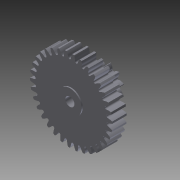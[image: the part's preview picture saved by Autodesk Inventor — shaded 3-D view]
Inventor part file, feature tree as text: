
AUTODESK INVENTOR PART (.ipt)
format: ipt  version: 2013 (Build 170138000, 138)  size: 1,623,040 bytes
history: native  units: in
note: dims shown in document units (in); Inventor stores cm internally (conversion verified against a paired STEP export)
features: extrude x4, sketch x3, plane x1, hole x1, fillet x1, projected_geometry x1
ambient origin geometry x8: Origin, YZ Plane, XZ Plane, XY Plane, X Axis, Y Axis, Z Axis, Center Point
bodies: Solid1 (feature_tree)
feature tree (11):
  sketch  "Sketch1"  dims[d0=0.098in d1=0.0in d2=0.008in d3=0.0in]
  extrude  "Extrusion1"  Depth=0.008in TaperAngle=0.0deg
  extrude  "Extrusion2"  Depth=0.008in TaperAngle=0.0deg
  plane  "Work Plane1"
  sketch  "Sketch2"  dims[d4=0.157in d5=0.008in d6=0.0in]
  extrude  "Extrusion3"  Depth=0.005in
  extrude  "Extrusion4"  [1 undecoded]
  hole  "Hole1"  [1 undecoded]
  fillet  "Fillet1"  [1 undecoded]
  projected_geometry  "Projected Loop1"
  sketch  "Sketch3"  dims[d7=0.008in d8=0.0in d9=0.061in d10=0.75in d11=0.375in d12=0.25in d13=0.5635in d14=1.0in d15=0.8108in d16=0.005in]
note: 3 required parameter values undecoded (feature->parameter linkage not recoverable at this tier; creation-order binding heuristic only, values carry confidence <= 0.55)
